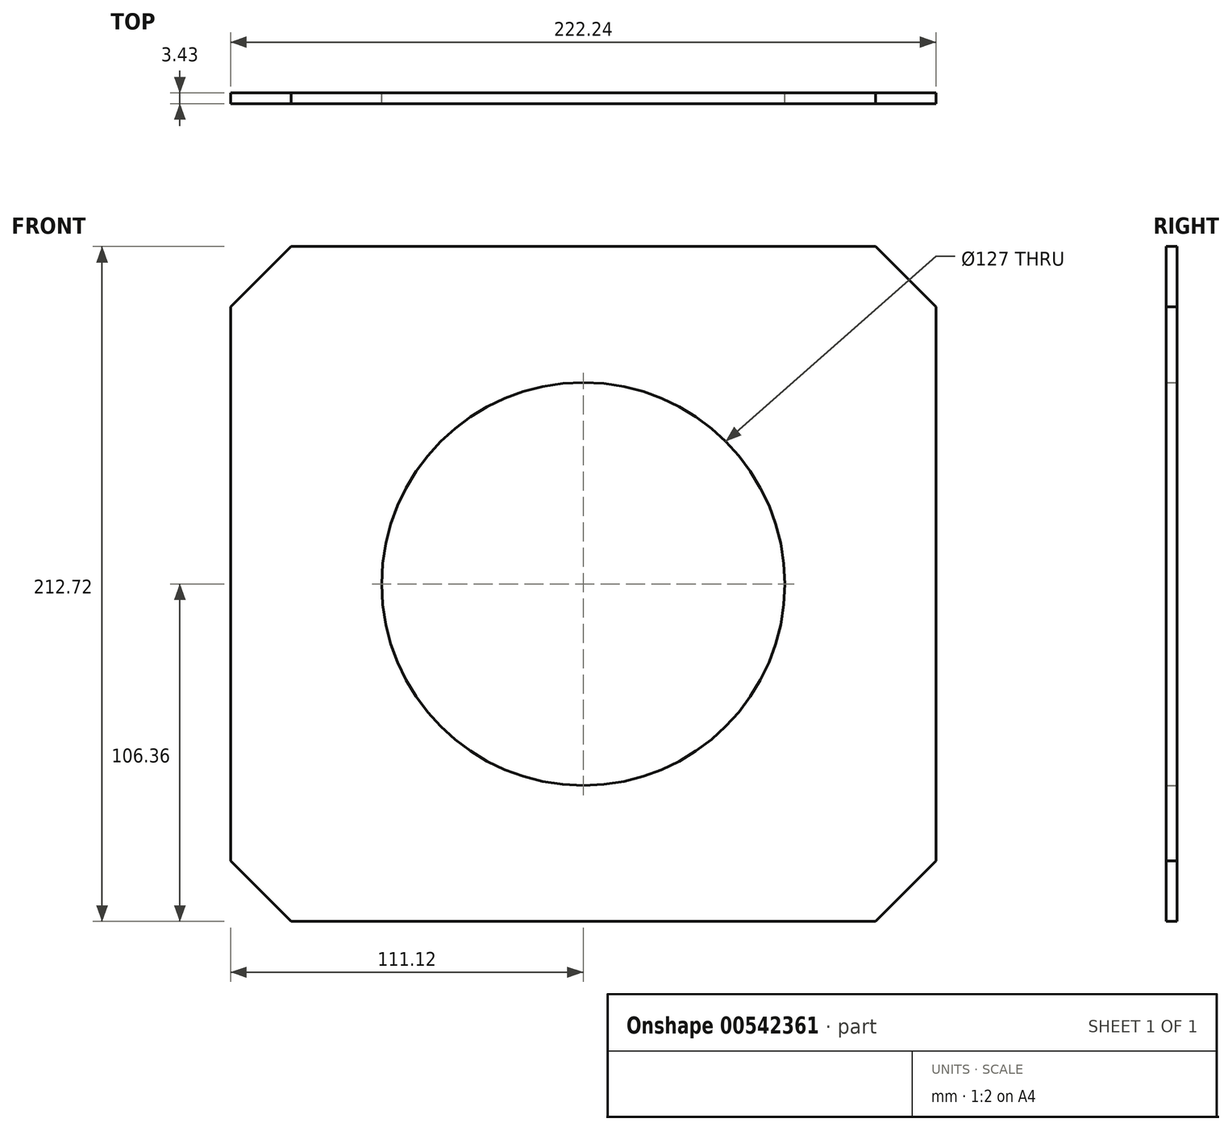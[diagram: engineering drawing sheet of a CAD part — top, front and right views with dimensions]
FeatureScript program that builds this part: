
annotation { "Feature Type Name" : "Feature", "Feature Type Description" : "" }
export const myFeature = defineFeature(function(context is Context, id is Id, definition is map)
    precondition{}
    {
        {
            var Q0;
            Q0=qCreatedBy(makeId("Front.planeOp"),FACE);
            var sketch = newSketch(context, id + "F0", { "sketchPlane" : qUnion([Q0])});
            skLineSegment(sketch, "E0.bottom", {"start": v(111.13, -106.36) * mm, "end": v(-111.13, -106.36) * mm});
            skLineSegment(sketch, "E0.top", {"start": v(111.13, 106.36) * mm, "end": v(-111.13, 106.36) * mm});
            skLineSegment(sketch, "E0.left", {"start": v(111.13, -106.36) * mm, "end": v(111.13, 106.36) * mm});
            skLineSegment(sketch, "E0.right", {"start": v(-111.13, -106.36) * mm, "end": v(-111.13, 106.36) * mm});
            skPoint(sketch, "E0.middle", {"position": v(0, 0) * mm});
            skCircle(sketch, "E1", {"center": v(0, 0) * mm, "radius": 63.5 * mm});
            skSolve(sketch);
        }
        {
            var Q0;
            Q0=makeQuery(id+"F0.imprint","IMPRINT",FACE,{"disambiguationData":[TD([[makeQuery(id+"F0.imprint","IMPRINT",EDGE,{"derivedFrom":sQuery(id+"F0.wireOp",EDGE,"E0.bottom")}),-1.0]])]});
            extrude(context, id + "F1", {"entities" : qUnion([Q0]), "depth" : 3.43 * mm, "offsetDistance" : 25.4 * mm});
        }
        {
            var Q0;
            Q0=makeQuery(id+"F1.opExtrude","SWEPT_EDGE",EDGE,{"disambiguationData":[OSD([sQuery(id+"F0.wireOp",EDGE,"E0.top"),sQuery(id+"F0.wireOp",EDGE,"E0.right")])]});
            var Q1;
            Q1=makeQuery(id+"F1.opExtrude","SWEPT_EDGE",EDGE,{"disambiguationData":[OSD([sQuery(id+"F0.wireOp",EDGE,"E0.top"),sQuery(id+"F0.wireOp",EDGE,"E0.left")])]});
            var Q2;
            Q2=makeQuery(id+"F1.opExtrude","SWEPT_EDGE",EDGE,{"disambiguationData":[OSD([sQuery(id+"F0.wireOp",EDGE,"E0.bottom"),sQuery(id+"F0.wireOp",EDGE,"E0.right")])]});
            var Q3;
            Q3=makeQuery(id+"F1.opExtrude","SWEPT_EDGE",EDGE,{"disambiguationData":[OSD([sQuery(id+"F0.wireOp",EDGE,"E0.bottom"),sQuery(id+"F0.wireOp",EDGE,"E0.left")])]});
            chamfer(context, id + "F2", {"entities" : qUnion([Q0, Q1, Q2, Q3]), "width" : 19.05 * mm, "tangentPropagation" : true});
        }
    });
